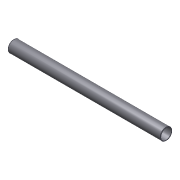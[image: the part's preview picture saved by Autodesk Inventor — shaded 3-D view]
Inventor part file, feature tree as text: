
AUTODESK INVENTOR PART (.ipt)
format: ipt  version: 2012 (Build 160160000, 160)  size: 110,592 bytes
history: native  units: in
note: dims shown in document units (in); Inventor stores cm internally (conversion verified against a paired STEP export)
features: other x42, revolve x1, sketch x1
ambient origin geometry x8: Origin, YZ Plane, XZ Plane, XY Plane, X Axis, Y Axis, Z Axis, Center Point
bodies: Solid1 (feature_tree)
feature tree (44):
  revolve  "Revolution1"  [1 undecoded]
  other  "tube_front_XY"
  other  "tube_front_YZ"
  other  "tube_front_ZX"
  other  "tube_front_X"
  other  "tube_front_Y"
  other  "tube_front_Z"
  other  "tube_front_Center"
  other  "tube_rear_XY"
  other  "tube_rear_YZ"
  other  "tube_rear_ZX"
  other  "tube_rear_X"
  other  "tube_rear_Y"
  other  "tube_rear_Z"
  other  "tube_rear_Center"
  other  "cp1_XY"
  other  "cp1_YZ"
  other  "cp1_ZX"
  other  "cp1_X"
  other  "cp1_Y"
  other  "cp1_Z"
  other  "cp1_Center"
  other  "cp2_XY"
  other  "cp2_YZ"
  other  "cp2_ZX"
  other  "cp2_X"
  other  "cp2_Y"
  other  "cp2_Z"
  other  "cp2_Center"
  other  "cp3_XY"
  other  "cp3_YZ"
  other  "cp3_ZX"
  other  "cp3_X"
  other  "cp3_Y"
  other  "cp3_Z"
  other  "cp3_Center"
  other  "cp4_XY"
  other  "cp4_YZ"
  other  "cp4_ZX"
  other  "cp4_X"
  other  "cp4_Y"
  other  "cp4_Z"
  other  "cp4_Center"
  sketch  "Sketch_1"  dims[d0=360.0deg]
note: 1 required parameter value undecoded (feature->parameter linkage not recoverable at this tier; creation-order binding heuristic only, values carry confidence <= 0.55)
